# Revit family: dc5d60c1_4a95_4bfe_80ec_93923bd6d959
name_source: partatom
category: Plumbing Fixtures
revit_build: Autodesk Revit 2015 (Build: 20140903_1530(x64)
units: mm (PartAtom-declared; Revit-internal decimal feet)

## types (1)
- Default
    BIMobject category = Valves
    BIMobject category code = plumbing-valves
    BIMobject main category = Plumbing
    BIMobject main category code = plumbing
    BOSUseNativeGeometries = 1
    Brand url = http://www.hansgrohe-int.com
    Design country = Germany
    EAN code = https://4059625105009
    Edition number = 1
    IFC Classification = Valve
    Installation instructions = https://pro.hansgrohe-int.com
    Manufacturer country = Germany
    Manufacturer name = hansgrohe
    Masterformat 2014 Code = 40 05 89
    Masterformat 2014 Description = Valve Accessories
    Material main = Chrome
    NBS Reference Code = 94-93
    NBS Reference Description = Valve Accessories
    Nominal height = 0
    Nominal width = 0
    OmniClass Code = 23-27 31 00
    OmniClass Description = Valves
    Product Guid = ae86056f-6763-482c-b15b-ab750dcbcffe
    Product SKU = 43927000
    Product data url = https://bimobject.com
    Product family = Waste systems sink
    Product group = Waste systems sink
    Product name = 43927000 D16-10 manual waste and overflow set for single bowl granite 43927000
    Product url = https://pro.hansgrohe-int.com
    QR code = http://bimobject.com
    Technical description = https://pro.hansgrohe-int.com
    UNSPSC Code = 40141616
    Uniclass 1.4 Code = L7136
    Uniclass 1.4 Description = Valves
    Uniclass 2.0 Code = PR-94-93
    Uniclass 2.0 Description = Valve Accessories
    Uniclass 2015 Code = Pr_65_54
    Uniclass 2015 Name = Valve products
    Uniformat II Code = D20
    Uniformat II Description = PLUMBING
    Weight Net (Kg) = 0

## geometry (parser evidence)
native form markers: Sweep x51
no freeform markers — native parametric forms only
